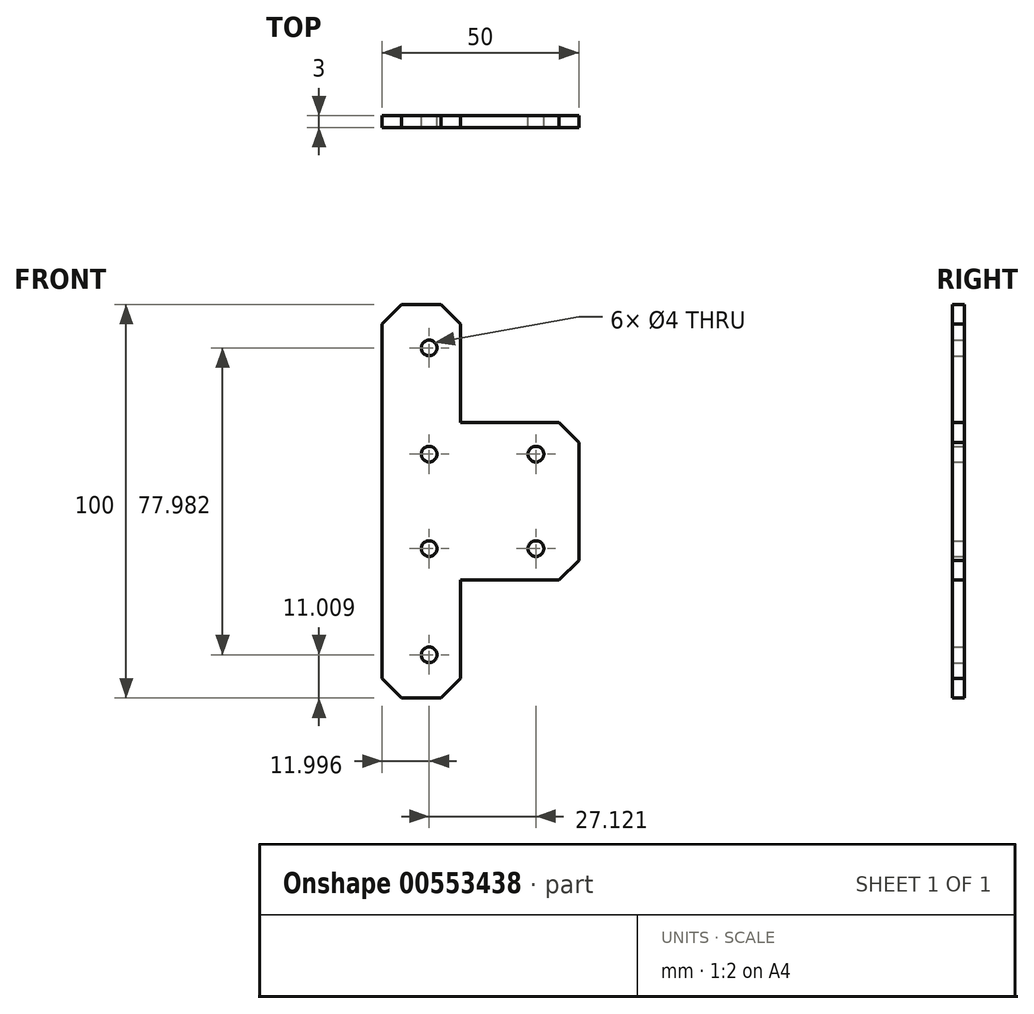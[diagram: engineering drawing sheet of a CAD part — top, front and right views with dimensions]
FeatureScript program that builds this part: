
annotation { "Feature Type Name" : "Feature", "Feature Type Description" : "" }
export const myFeature = defineFeature(function(context is Context, id is Id, definition is map)
    precondition{}
    {
        {
            var Q0;
            Q0=qCreatedBy(makeId("Front.planeOp"),FACE);
            var sketch = newSketch(context, id + "F0", { "sketchPlane" : qUnion([Q0])});
            skLineSegment(sketch, "E0", {"start": v(-55.77, 50) * mm, "end": v(-55.77, 0) * mm});
            skLineSegment(sketch, "E1", {"start": v(-55.77, 0) * mm, "end": v(-5.77, 0) * mm});
            skLineSegment(sketch, "E2", {"start": v(-5.77, 0) * mm, "end": v(-5.77, 20) * mm});
            skLineSegment(sketch, "E3", {"start": v(-5.77, 20) * mm, "end": v(-35.77, 20) * mm});
            skLineSegment(sketch, "E4", {"start": v(-35.77, 20) * mm, "end": v(-35.77, 50) * mm});
            skLineSegment(sketch, "E5", {"start": v(-35.77, 50) * mm, "end": v(-55.77, 50) * mm});
            skCircle(sketch, "E6", {"center": v(-43.77, 39) * mm, "radius": 2 * mm});
            skPoint(sketch, "E6.centerSnap0", {"position": v(-45.77, 50) * mm});
            skCircle(sketch, "E7", {"center": v(-16.65, 12) * mm, "radius": 2 * mm});
            skPoint(sketch, "E7.centerSnap0", {"position": v(-5.77, 10) * mm});
            skCircle(sketch, "E8", {"center": v(-43.77, 12) * mm, "radius": 2 * mm});
            skSolve(sketch);
        }
        {
            var Q0;
            Q0=qSketchRegion(id+"F0",true);
            extrude(context, id + "F1", {"entities" : qUnion([Q0]), "depth" : 3 * mm, "offsetDistance" : 25 * mm});
        }
        {
            var Q0;
            Q0=makeQuery(id+"F1.opExtrude","SWEPT_BODY",BODY,{"disambiguationData":[OSD([sQuery(id+"F0.wireOp",EDGE,"E0"),sQuery(id+"F0.wireOp",EDGE,"E1"),sQuery(id+"F0.wireOp",EDGE,"E2"),sQuery(id+"F0.wireOp",EDGE,"E3"),sQuery(id+"F0.wireOp",EDGE,"E4"),sQuery(id+"F0.wireOp",EDGE,"E5"),sQuery(id+"F0.wireOp",EDGE,"E6"),sQuery(id+"F0.wireOp",EDGE,"E7"),sQuery(id+"F0.wireOp",EDGE,"E8")])]});
            var Q1;
            Q1=makeQuery(id+"F1.opExtrude","SWEPT_FACE",FACE,{"disambiguationData":[OSD([sQuery(id+"F0.wireOp",EDGE,"E1")])]});
            mirror(context, id + "F2", {"operationType" : NewBodyOperationType.ADD, "entities" : qUnion([Q0]), "mirrorPlane" : qUnion([Q1])});
        }
        {
            var Q0;
            Q0=makeQuery(id+"F1.opExtrude","SWEPT_EDGE",EDGE,{"disambiguationData":[OSD([sQuery(id+"F0.wireOp",EDGE,"E2"),sQuery(id+"F0.wireOp",EDGE,"E3")])]});
            var Q1;
            Q1=makeQuery(id+"F2.opPattern","COPY",EDGE,{"derivedFrom":makeQuery(id+"F1.opExtrude","SWEPT_EDGE",EDGE,{"disambiguationData":[OSD([sQuery(id+"F0.wireOp",EDGE,"E2"),sQuery(id+"F0.wireOp",EDGE,"E3")])]}),"instanceName":"1"});
            var Q2;
            Q2=makeQuery(id+"F1.opExtrude","SWEPT_EDGE",EDGE,{"disambiguationData":[OSD([sQuery(id+"F0.wireOp",EDGE,"E4"),sQuery(id+"F0.wireOp",EDGE,"E5")])]});
            var Q3;
            Q3=makeQuery(id+"F2.opPattern","COPY",EDGE,{"derivedFrom":makeQuery(id+"F1.opExtrude","SWEPT_EDGE",EDGE,{"disambiguationData":[OSD([sQuery(id+"F0.wireOp",EDGE,"E4"),sQuery(id+"F0.wireOp",EDGE,"E5")])]}),"instanceName":"1"});
            var Q4;
            Q4=makeQuery(id+"F1.opExtrude","SWEPT_EDGE",EDGE,{"disambiguationData":[OSD([sQuery(id+"F0.wireOp",EDGE,"E0"),sQuery(id+"F0.wireOp",EDGE,"E5")])]});
            var Q5;
            Q5=makeQuery(id+"F2.opPattern","COPY",EDGE,{"derivedFrom":makeQuery(id+"F1.opExtrude","SWEPT_EDGE",EDGE,{"disambiguationData":[OSD([sQuery(id+"F0.wireOp",EDGE,"E0"),sQuery(id+"F0.wireOp",EDGE,"E5")])]}),"instanceName":"1"});
            chamfer(context, id + "F3", {"entities" : qUnion([Q0, Q1, Q2, Q3, Q4, Q5]), "width" : 5 * mm, "tangentPropagation" : true});
        }
    });
